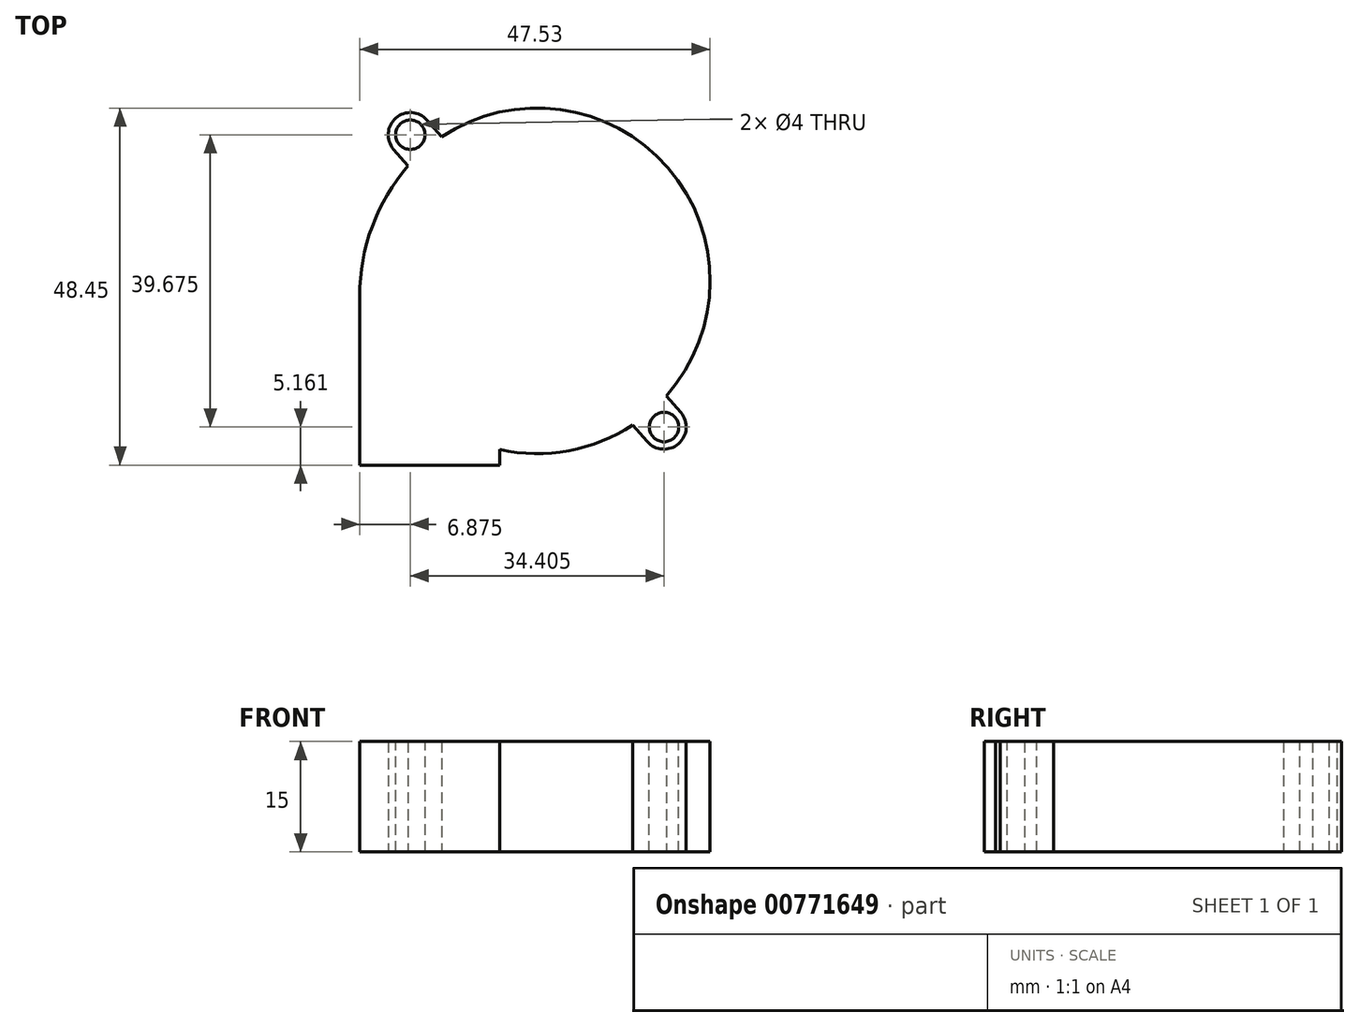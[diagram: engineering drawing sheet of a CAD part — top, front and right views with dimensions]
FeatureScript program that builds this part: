
annotation { "Feature Type Name" : "Feature", "Feature Type Description" : "" }
export const myFeature = defineFeature(function(context is Context, id is Id, definition is map)
    precondition{}
    {
        {
            var Q0;
            Q0=qCreatedBy(makeId("Top.planeOp"),FACE);
            var sketch = newSketch(context, id + "F0", { "sketchPlane" : qUnion([Q0])});
            skPoint(sketch, "E0.middle", {"position": v(0, 0) * mm});
            skLineSegment(sketch, "E1", {"start": v(-24.08, -2.02) * mm, "end": v(-24.08, -25) * mm});
            skLineSegment(sketch, "E2", {"start": v(-5.08, -25) * mm, "end": v(-5.08, -22.9) * mm});
            skLineSegment(sketch, "E3", {"start": v(-5.08, -25) * mm, "end": v(-24.08, -25) * mm});
            skArc(sketch, "E4", {"start": v(-5.08, -22.9) * mm, "mid": v(4.28, -23.06) * mm, "end": v(12.97, -19.54) * mm});
            skLineSegment(sketch, "E5", {"start": v(12.97, -19.54) * mm, "end": v(14.93, -21.8) * mm});
            skLineSegment(sketch, "E6", {"start": v(17.5, -15.6) * mm, "end": v(19.47, -17.87) * mm});
            skCircle(sketch, "E7", {"center": v(0, 0) * mm, "radius": 23.45 * mm, "construction": true});
            skLineSegment(sketch, "E8", {"start": v(17.2, -19.84) * mm, "end": v(0, 0) * mm, "construction": true});
            skLineSegment(sketch, "E9", {"start": v(0, 0) * mm, "end": v(24.56, 21.3) * mm, "construction": true});
            skLineSegment(sketch, "E10", {"start": v(0, 0) * mm, "end": v(-21.83, -18.92) * mm, "construction": true});
            skArc(sketch, "E11", {"start": v(14.93, -21.8) * mm, "mid": v(19.17, -22.1) * mm, "end": v(19.47, -17.87) * mm});
            skLineSegment(sketch, "E12", {"start": v(-17.5, 15.6) * mm, "end": v(-19.47, 17.87) * mm});
            skLineSegment(sketch, "E13", {"start": v(-12.97, 19.53) * mm, "end": v(-14.94, 21.8) * mm});
            skArc(sketch, "E14", {"start": v(-14.94, 21.8) * mm, "mid": v(-19.17, 22.1) * mm, "end": v(-19.47, 17.87) * mm});
            skLineSegment(sketch, "E15", {"start": v(0, 0) * mm, "end": v(-17.2, 19.84) * mm, "construction": true});
            skArc(sketch, "E16", {"start": v(-17.5, 15.6) * mm, "mid": v(-22.38, 7.38) * mm, "end": v(-24.08, -2.02) * mm});
            skArc(sketch, "E17", {"start": v(17.5, -15.6) * mm, "mid": v(17.72, 15.36) * mm, "end": v(-12.97, 19.53) * mm});
            skSolve(sketch);
        }
        {
            var Q0;
            Q0 = qSketchRegion(id + "F0", true);
            extrude(context, id + "F1", {"entities" : qUnion([Q0]), "depth" : 15 * mm, "offsetDistance" : 25 * mm});
        }
        {
            var Q0;
            Q0=makeQuery(id+"F1.opExtrude","CAP_FACE",FACE,{"disambiguationData":[OSD([sQuery(id+"F0.wireOp",EDGE,"E1"),sQuery(id+"F0.wireOp",EDGE,"E2"),sQuery(id+"F0.wireOp",EDGE,"E3"),sQuery(id+"F0.wireOp",EDGE,"E4"),sQuery(id+"F0.wireOp",EDGE,"E5"),sQuery(id+"F0.wireOp",EDGE,"E6"),sQuery(id+"F0.wireOp",EDGE,"E11"),sQuery(id+"F0.wireOp",EDGE,"E12"),sQuery(id+"F0.wireOp",EDGE,"E13"),sQuery(id+"F0.wireOp",EDGE,"E14"),sQuery(id+"F0.wireOp",EDGE,"E16"),sQuery(id+"F0.wireOp",EDGE,"E17")])],"isStart":false});
            var sketch = newSketch(context, id + "F2", { "sketchPlane" : qUnion([Q0])});
            skCircle(sketch, "E18", {"center": v(17.2, -19.84) * mm, "radius": 2 * mm});
            skCircle(sketch, "E19", {"center": v(-17.2, 19.84) * mm, "radius": 2 * mm});
            skSolve(sketch);
        }
        {
            var Q0;
            Q0 = qSketchRegion(id + "F2", true);
            extrude(context, id + "F3", {"entities" : qUnion([Q0]), "operationType" : NewBodyOperationType.REMOVE, "endBound" : BoundingType.UP_TO_NEXT, "oppositeDirection" : true, "depth" : 25 * mm, "offsetDistance" : 25 * mm});
        }
    });
